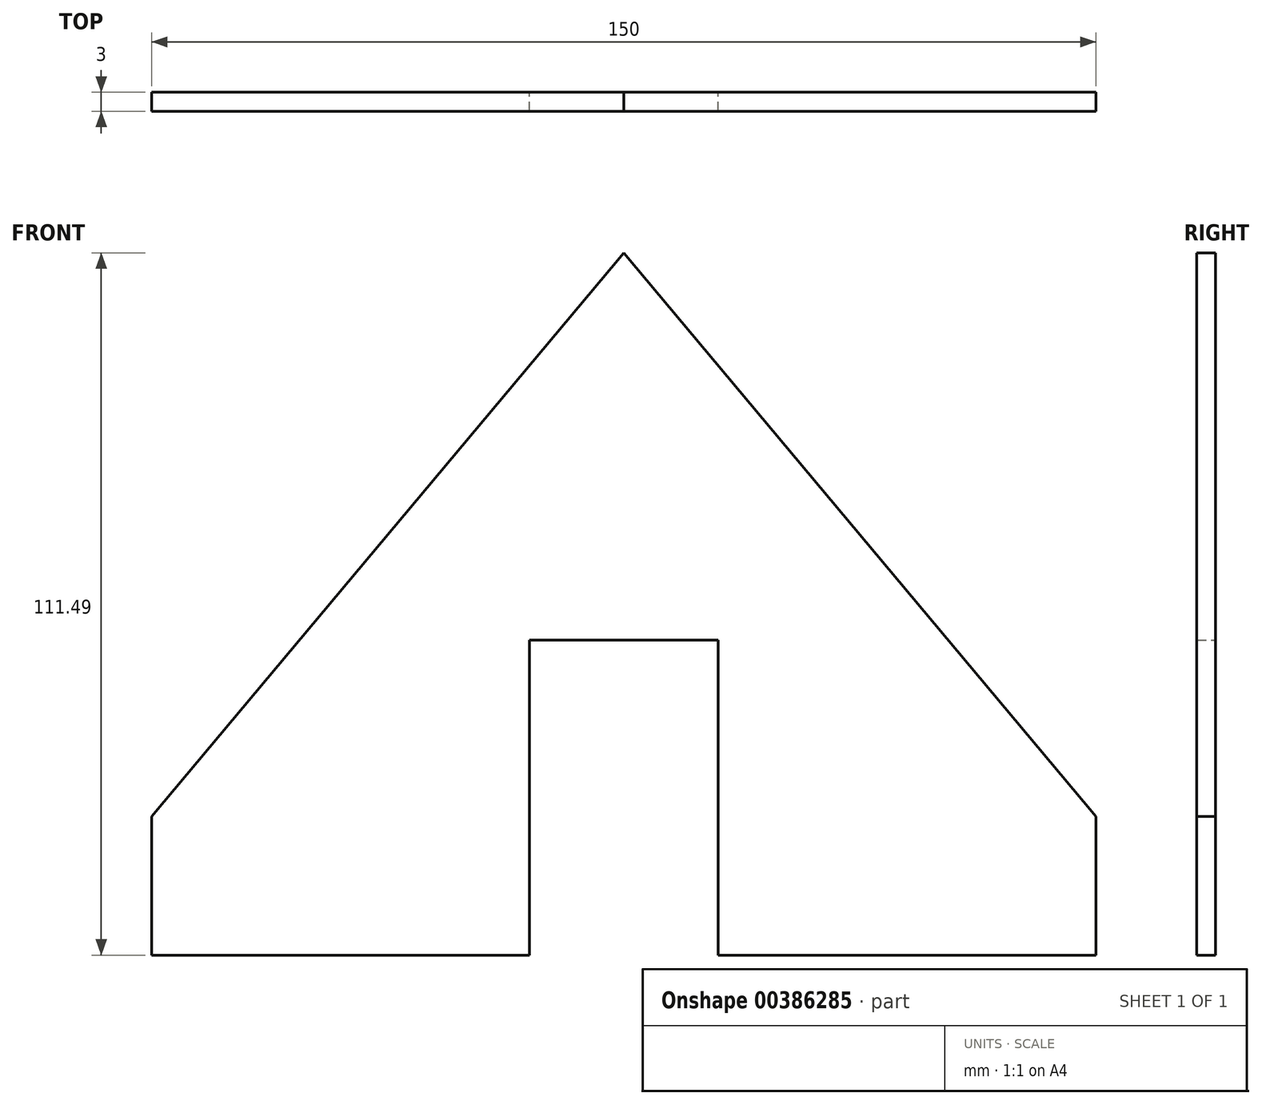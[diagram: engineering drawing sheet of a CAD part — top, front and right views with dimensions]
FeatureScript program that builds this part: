
annotation { "Feature Type Name" : "Feature", "Feature Type Description" : "" }
export const myFeature = defineFeature(function(context is Context, id is Id, definition is map)
    precondition{}
    {
        {
            var Q0;
            Q0=qCreatedBy(makeId("Front.planeOp"),FACE);
            var sketch = newSketch(context, id + "F0", { "sketchPlane" : qUnion([Q0])});
            skLineSegment(sketch, "E0.bottom", {"start": v(-10.56, 22) * mm, "end": v(139.44, 22) * mm});
            skLineSegment(sketch, "E0.top", {"start": v(-10.56, 0) * mm, "end": v(139.44, 0) * mm});
            skLineSegment(sketch, "E0.left", {"start": v(-10.56, 22) * mm, "end": v(-10.56, 0) * mm});
            skLineSegment(sketch, "E0.right", {"start": v(139.44, 22) * mm, "end": v(139.44, 0) * mm});
            skCircle(sketch, "E1.cCircle", {"center": v(64.44, 57) * mm, "radius": 35 * mm, "construction": true});
            skLineSegment(sketch, "E1.0", {"start": v(139.44, 22) * mm, "end": v(-10.56, 22) * mm});
            skLineSegment(sketch, "E1.1", {"start": v(-10.56, 22) * mm, "end": v(64.44, 111.49) * mm});
            skLineSegment(sketch, "E1.2", {"start": v(64.44, 111.49) * mm, "end": v(139.44, 22) * mm});
            skPoint(sketch, "E1.0.midPoint", {"position": v(64.44, 22) * mm});
            skLineSegment(sketch, "E2.bottom", {"start": v(49.44, 50) * mm, "end": v(79.44, 50) * mm});
            skLineSegment(sketch, "E2.top", {"start": v(49.44, 0) * mm, "end": v(79.44, 0) * mm});
            skLineSegment(sketch, "E2.left", {"start": v(49.44, 50) * mm, "end": v(49.44, 0) * mm});
            skLineSegment(sketch, "E2.right", {"start": v(79.44, 50) * mm, "end": v(79.44, 0) * mm});
            skSolve(sketch);
        }
        {
            var Q0;
            {var subQ0=sQuery(id+"F0.wireOp",EDGE,"E0.left");Q0=makeQuery(id+"F0.imprint","IMPRINT",FACE,{"disambiguationData":[TD([[makeQuery(id+"F0.imprint","IMPRINT",EDGE,{"derivedFrom":subQ0}),1.0]])]});}
            var Q1;
            {var subQ1=sQuery(id+"F0.wireOp",EDGE,"E1.1");Q1=makeQuery(id+"F0.imprint","IMPRINT",FACE,{"disambiguationData":[TD([[makeQuery(id+"F0.imprint","IMPRINT",EDGE,{"derivedFrom":subQ1}),-1.0]])]});}
            var Q2;
            {var subQ0=sQuery(id+"F0.wireOp",EDGE,"E0.right");Q2=makeQuery(id+"F0.imprint","IMPRINT",FACE,{"disambiguationData":[TD([[makeQuery(id+"F0.imprint","IMPRINT",EDGE,{"derivedFrom":subQ0}),-1.0]])]});}
            extrude(context, id + "F1", {"entities" : qUnion([Q0, Q1, Q2]), "depth" : 3 * mm});
        }
    });
